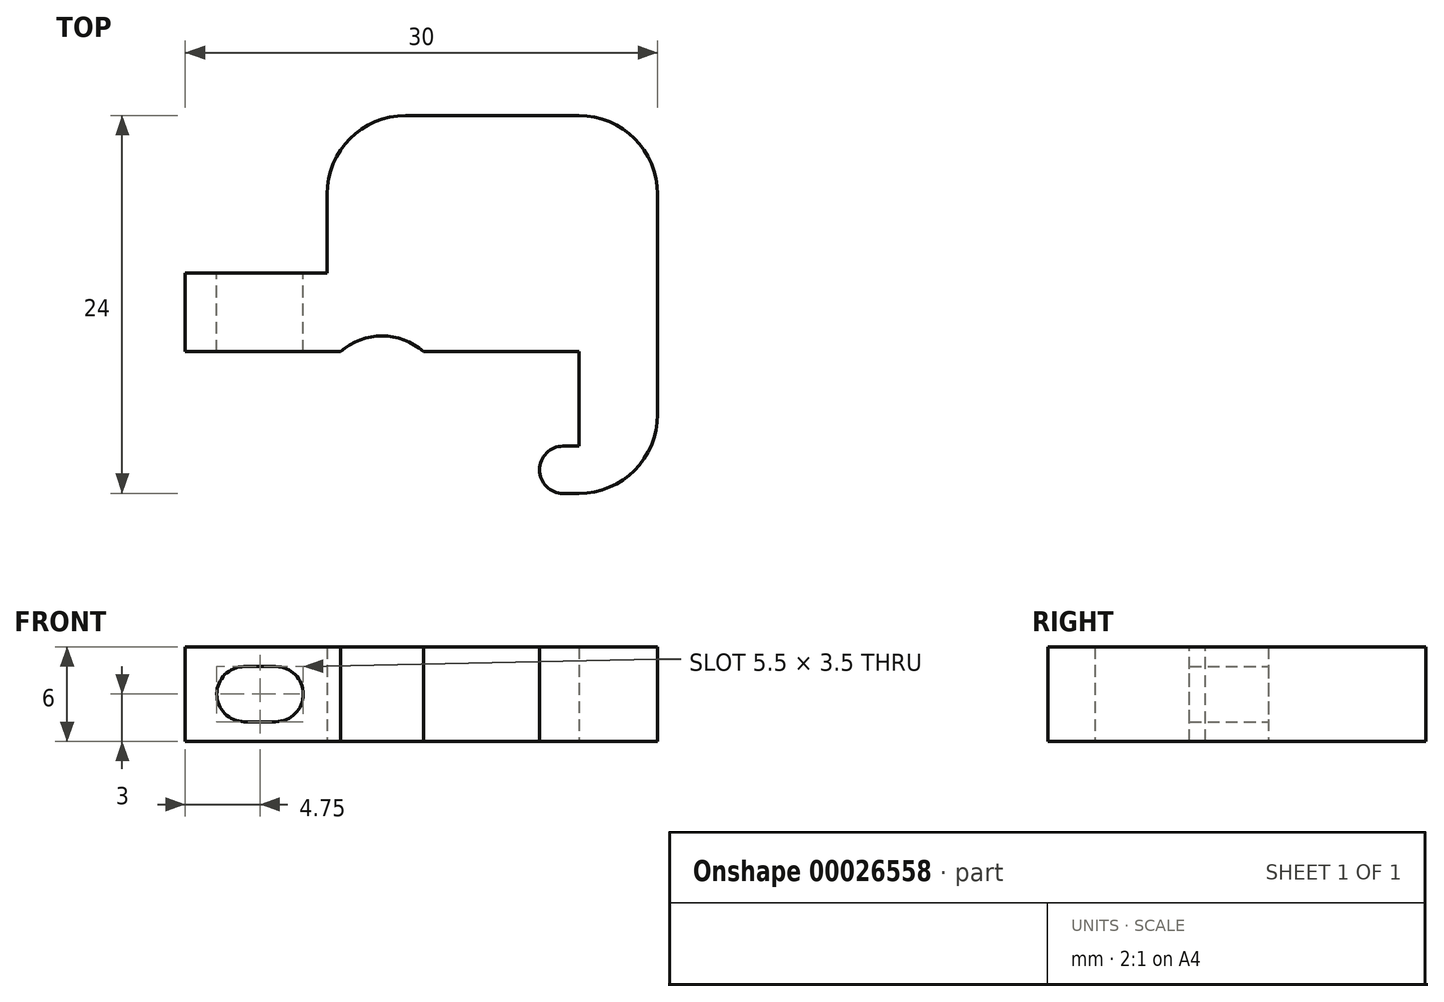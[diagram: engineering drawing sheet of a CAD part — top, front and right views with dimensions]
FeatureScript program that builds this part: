
annotation { "Feature Type Name" : "Feature", "Feature Type Description" : "" }
export const myFeature = defineFeature(function(context is Context, id is Id, definition is map)
    precondition{}
    {
        {
            var Q0;
            Q0=qCreatedBy(makeId("Top.planeOp"),FACE);
            var sketch = newSketch(context, id + "F0", { "sketchPlane" : qUnion([Q0])});
            skLineSegment(sketch, "E0", {"start": v(0, 0) * mm, "end": v(5, 0) * mm});
            skLineSegment(sketch, "E1", {"start": v(5, 0) * mm, "end": v(5, 14) * mm});
            skLineSegment(sketch, "E2", {"start": v(5, 14) * mm, "end": v(-25, 14) * mm});
            skLineSegment(sketch, "E3", {"start": v(-25, 14) * mm, "end": v(-25, 9) * mm});
            skLineSegment(sketch, "E4", {"start": v(-25, 9) * mm, "end": v(0, 9) * mm});
            skLineSegment(sketch, "E5", {"start": v(0, 9) * mm, "end": v(0, 3) * mm});
            skLineSegment(sketch, "E6", {"start": v(0, 3) * mm, "end": v(-1, 3) * mm});
            skLineSegment(sketch, "E7", {"start": v(0, 0) * mm, "end": v(-1, 0) * mm});
            skArc(sketch, "E8", {"start": v(-1, 3) * mm, "mid": v(-2.5, 1.5) * mm, "end": v(-1, 0) * mm});
            skSolve(sketch);
        }
        {
            var Q0;
            Q0=qSketchRegion(id+"F0",true);
            extrude(context, id + "F1", {"entities" : qUnion([Q0]), "depth" : 6 * mm});
        }
        {
            var Q0;
            Q0=makeQuery(id+"F1.opExtrude","SWEPT_FACE",FACE,{"disambiguationData":[OSD([sQuery(id+"F0.wireOp",EDGE,"E2")])]});
            var sketch = newSketch(context, id + "F2", { "sketchPlane" : qUnion([Q0])});
            skCircle(sketch, "E9", {"center": v(21.25, 3) * mm, "radius": 1.75 * mm});
            skLineSegment(sketch, "E10", {"start": v(21.25, 6) * mm, "end": v(21.25, 0) * mm});
            skCircle(sketch, "E11", {"center": v(19.25, 3) * mm, "radius": 1.75 * mm});
            skLineSegment(sketch, "E12", {"start": v(19.25, 4.75) * mm, "end": v(21.25, 4.75) * mm});
            skLineSegment(sketch, "E13", {"start": v(19.25, 1.25) * mm, "end": v(21.25, 1.25) * mm});
            skSolve(sketch);
        }
        {
            var Q0;
            Q0=qSketchRegion(id+"F2",true);
            var Q1;
            {var subQ0=sQuery(id+"F2.wireOp",EDGE,"E11");var subQ1=sQuery(id+"F2.wireOp",EDGE,"E9");var subQ3=makeQuery(id+"F2.imprint","INTERSECT",VERTEX,{"disambiguationData":[OD(0.0)],"derivedFrom":[subQ1,subQ0]});Q1=makeQuery(id+"F2.imprint","IMPRINT",FACE,{"disambiguationData":[TD([[makeQuery(id+"F2.imprint","IMPRINT",EDGE,{"disambiguationData":[TD([[subQ3,-1.0]])],"derivedFrom":subQ1}),1.0]])]});}
            extrude(context, id + "F3", {"entities" : qUnion([Q0, Q1]), "operationType" : NewBodyOperationType.REMOVE, "oppositeDirection" : true, "depth" : 25 * mm, "hasSecondDirection" : true, "secondDirectionOppositeDirection" : false, "secondDirectionDepth" : 25 * mm});
        }
        {
            var Q0;
            Q0=makeQuery(id+"F1.opExtrude","SWEPT_FACE",FACE,{"disambiguationData":[OSD([sQuery(id+"F0.wireOp",EDGE,"E2")])]});
            var sketch = newSketch(context, id + "F4", { "sketchPlane" : qUnion([Q0])});
            skLineSegment(sketch, "E14.bottom", {"start": v(-5, 6) * mm, "end": v(16, 6) * mm});
            skLineSegment(sketch, "E14.top", {"start": v(-5, 0) * mm, "end": v(16, 0) * mm});
            skLineSegment(sketch, "E14.left", {"start": v(-5, 6) * mm, "end": v(-5, 0) * mm});
            skLineSegment(sketch, "E14.right", {"start": v(16, 6) * mm, "end": v(16, 0) * mm});
            skSolve(sketch);
        }
        {
            var Q0;
            Q0=qSketchRegion(id+"F4",true);
            extrude(context, id + "F5", {"entities" : qUnion([Q0]), "operationType" : NewBodyOperationType.ADD, "depth" : 10 * mm});
        }
        {
            var Q0;
            Q0=makeQuery(id+"F5.opExtrude","CAP_EDGE",EDGE,{"disambiguationData":[OSD([sQuery(id+"F4.wireOp",EDGE,"E14.left")])],"isStart":false});
            var Q1;
            Q1=makeQuery(id+"F5.opExtrude","CAP_EDGE",EDGE,{"disambiguationData":[OSD([sQuery(id+"F4.wireOp",EDGE,"E14.right")])],"isStart":false});
            fillet(context, id + "F6", {"entities" : qUnion([Q0, Q1]), "radius" : 5 * mm, "tangentPropagation" : true, "allowEdgeOverflow" : false});
        }
        {
            var Q0;
            Q0=makeQuery(id+"F1.opExtrude","SWEPT_EDGE",EDGE,{"disambiguationData":[OSD([sQuery(id+"F0.wireOp",EDGE,"E0"),sQuery(id+"F0.wireOp",EDGE,"E1")])]});
            fillet(context, id + "F7", {"entities" : qUnion([Q0]), "radius" : 5 * mm, "tangentPropagation" : true, "allowEdgeOverflow" : false});
        }
        {
            var Q0;
            Q0=makeQuery(id+"F5.boolean.opBoolean","MERGE",FACE,{"derivedFrom":[makeQuery(id+"F1.opExtrude","CAP_FACE",FACE,{"disambiguationData":[OSD([sQuery(id+"F0.wireOp",EDGE,"E0"),sQuery(id+"F0.wireOp",EDGE,"E1"),sQuery(id+"F0.wireOp",EDGE,"E2"),sQuery(id+"F0.wireOp",EDGE,"E3"),sQuery(id+"F0.wireOp",EDGE,"E4"),sQuery(id+"F0.wireOp",EDGE,"E5"),sQuery(id+"F0.wireOp",EDGE,"E6"),sQuery(id+"F0.wireOp",EDGE,"E7"),sQuery(id+"F0.wireOp",EDGE,"E8")])],"isStart":false}),makeQuery(id+"F5.opExtrude","SWEPT_FACE",FACE,{"disambiguationData":[OSD([sQuery(id+"F4.wireOp",EDGE,"E14.bottom")])]})]});
            var sketch = newSketch(context, id + "F8", { "sketchPlane" : qUnion([Q0])});
            skLineSegment(sketch, "E15", {"start": v(-12.5, -1.14) * mm, "end": v(-12.5, 9) * mm, "construction": true});
            skArc(sketch, "E16", {"start": v(-9.85, 9) * mm, "mid": v(-12.5, 10) * mm, "end": v(-15.15, 9) * mm});
            skLineSegment(sketch, "E17", {"start": v(-15.15, 9) * mm, "end": v(-9.85, 9) * mm});
            skSolve(sketch);
        }
        {
            var Q0;
            Q0=makeQuery(id+"F8.imprint","IMPRINT",FACE,{"disambiguationData":[TD([[makeQuery(id+"F8.imprint","IMPRINT",EDGE,{"derivedFrom":sQuery(id+"F8.wireOp",EDGE,"E16")}),1.0]])]});
            extrude(context, id + "F9", {"entities" : qUnion([Q0]), "operationType" : NewBodyOperationType.REMOVE, "endBound" : BoundingType.UP_TO_NEXT, "oppositeDirection" : true, "depth" : 25 * mm});
        }
    });
